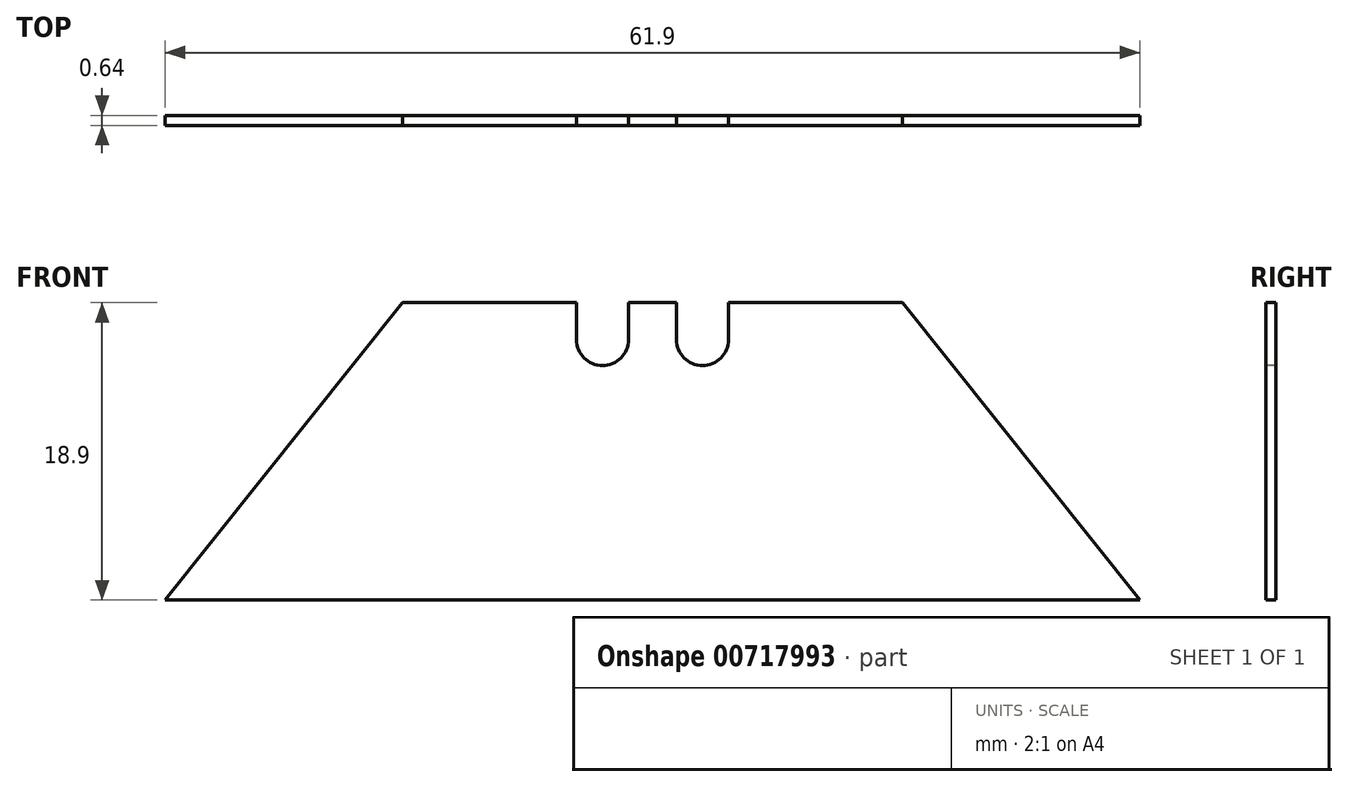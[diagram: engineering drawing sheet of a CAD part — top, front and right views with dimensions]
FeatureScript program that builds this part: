
annotation { "Feature Type Name" : "Feature", "Feature Type Description" : "" }
export const myFeature = defineFeature(function(context is Context, id is Id, definition is map)
    precondition{}
    {
        {
            var Q0;
            Q0=qCreatedBy(makeId("Front.planeOp"),FACE);
            var sketch = newSketch(context, id + "F0", { "sketchPlane" : qUnion([Q0])});
            skLineSegment(sketch, "E0", {"start": v(-15.88, 0) * mm, "end": v(15.88, 0) * mm});
            skLineSegment(sketch, "E1", {"start": v(15.87, 0) * mm, "end": v(30.95, -18.9) * mm});
            skLineSegment(sketch, "E2", {"start": v(30.95, -18.9) * mm, "end": v(-30.95, -18.9) * mm});
            skLineSegment(sketch, "E3", {"start": v(-30.95, -18.9) * mm, "end": v(-15.88, 0) * mm});
            skPoint(sketch, "E4", {"position": v(0, 0) * mm});
            skPoint(sketch, "E5", {"position": v(0, -18.9) * mm});
            skSolve(sketch);
        }
        {
            var Q0;
            Q0=makeQuery(id+"F0.imprint","IMPRINT",FACE,{"disambiguationData":[TD([[makeQuery(id+"F0.imprint","IMPRINT",EDGE,{"derivedFrom":sQuery(id+"F0.wireOp",EDGE,"E0")}),-1.0]])]});
            extrude(context, id + "F1", {"entities" : qUnion([Q0]), "endBound" : BoundingType.SYMMETRIC, "depth" : 0.64 * mm, "offsetDistance" : 25.4 * mm});
        }
        {
            var Q0;
            Q0=qCreatedBy(makeId("Front.planeOp"),FACE);
            var sketch = newSketch(context, id + "F2", { "sketchPlane" : qUnion([Q0])});
            skLineSegment(sketch, "E6", {"start": v(-4.83, 0) * mm, "end": v(-4.83, -2.35) * mm});
            skLineSegment(sketch, "E7", {"start": v(-1.53, -2.35) * mm, "end": v(-1.53, 0) * mm});
            skLineSegment(sketch, "E8", {"start": v(-1.52, 0) * mm, "end": v(-4.83, 0) * mm});
            skArc(sketch, "E9", {"start": v(-4.82, -2.35) * mm, "mid": v(-3.17, -4) * mm, "end": v(-1.52, -2.35) * mm});
            skLineSegment(sketch, "E10.MirrorCS", {"start": v(4.83, 0) * mm, "end": v(4.83, -2.35) * mm});
            skLineSegment(sketch, "E11.MirrorCS", {"start": v(1.52, 0) * mm, "end": v(4.83, 0) * mm});
            skLineSegment(sketch, "E12.MirrorCS", {"start": v(1.53, -2.35) * mm, "end": v(1.53, 0) * mm});
            skArc(sketch, "E13.MirrorCS", {"start": v(4.82, -2.35) * mm, "mid": v(3.17, -4) * mm, "end": v(1.52, -2.35) * mm});
            skSolve(sketch);
        }
        {
            var Q0;
            Q0 = qSketchRegion(id + "F2", true);
            extrude(context, id + "F3", {"entities" : qUnion([Q0]), "operationType" : NewBodyOperationType.REMOVE, "endBound" : BoundingType.THROUGH_ALL, "oppositeDirection" : true, "depth" : 25.4 * mm, "offsetDistance" : 25.4 * mm, "hasSecondDirection" : true, "secondDirectionBound" : SecondDirectionBoundingType.THROUGH_ALL, "secondDirectionOppositeDirection" : false, "secondDirectionDepth" : 25.4 * mm});
        }
    });
